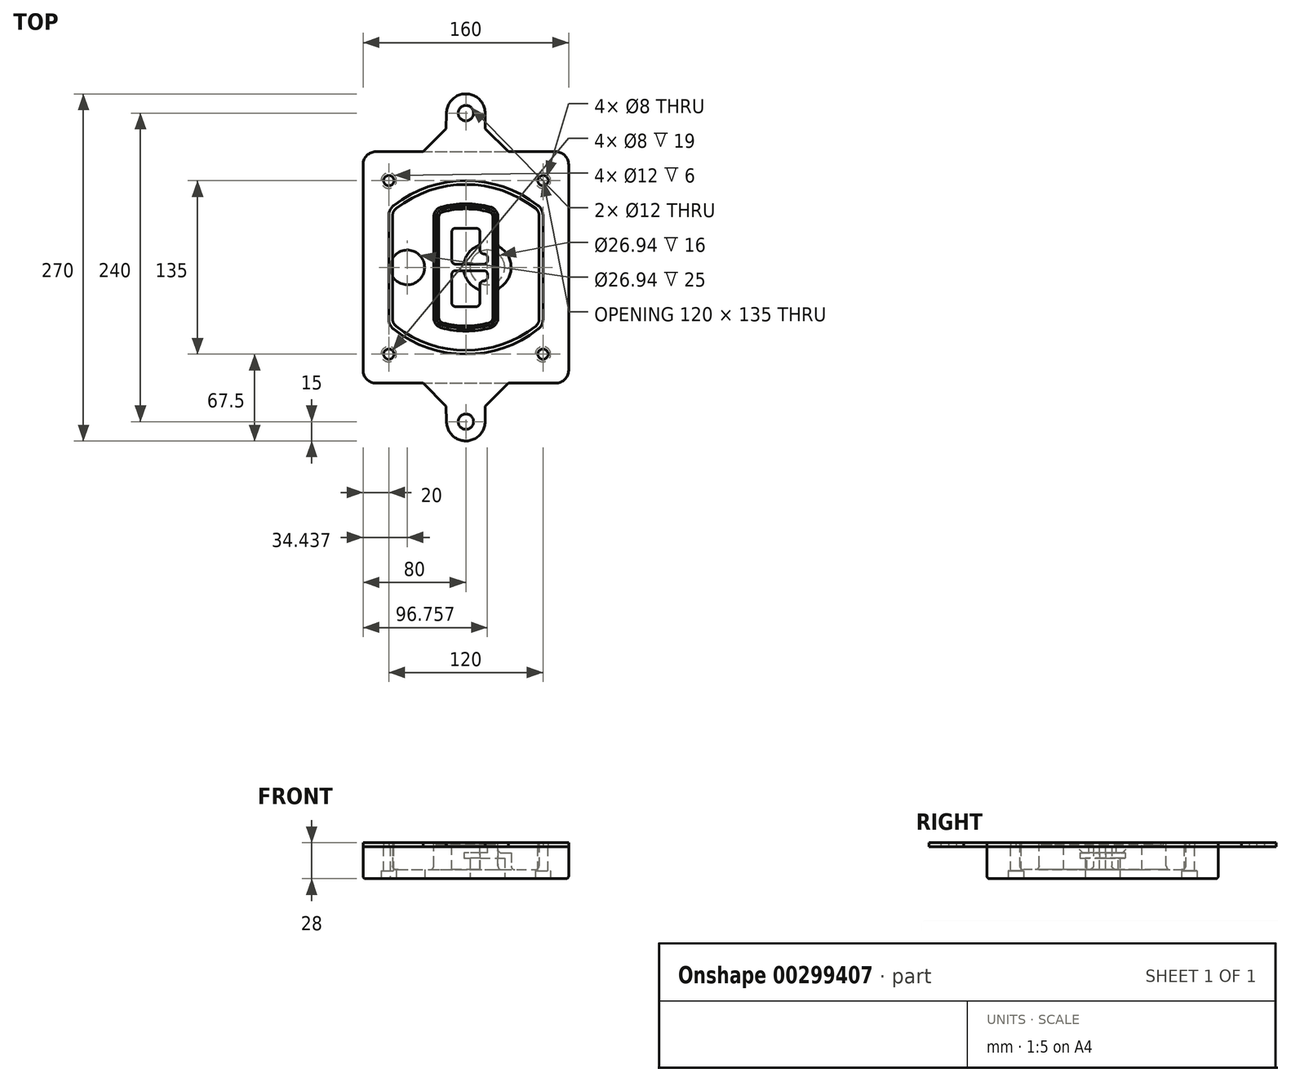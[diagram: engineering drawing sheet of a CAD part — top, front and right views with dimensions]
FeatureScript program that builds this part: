
annotation { "Feature Type Name" : "Feature", "Feature Type Description" : "" }
export const myFeature = defineFeature(function(context is Context, id is Id, definition is map)
    precondition{}
    {
        {
            var Q0;
            Q0=qCreatedBy(makeId("Top.planeOp"),FACE);
            var sketch = newSketch(context, id + "F0", { "sketchPlane" : qUnion([Q0])});
            skPoint(sketch, "E0.rect.middle", {"position": v(0, 0) * mm});
            skLineSegment(sketch, "E1.bottom", {"start": v(-70, -90) * mm, "end": v(70, -90) * mm});
            skLineSegment(sketch, "E1.top", {"start": v(-70, 90) * mm, "end": v(70, 90) * mm});
            skLineSegment(sketch, "E1.left", {"start": v(-80, -80) * mm, "end": v(-80, 80) * mm});
            skLineSegment(sketch, "E1.right", {"start": v(80, -80) * mm, "end": v(80, 80) * mm});
            skLineSegment(sketch, "E2", {"start": v(-80, 90) * mm, "end": v(80, -90) * mm, "construction": true});
            skLineSegment(sketch, "E3", {"start": v(80, 90) * mm, "end": v(-80, -90) * mm, "construction": true});
            skCircle(sketch, "E4", {"center": v(-60, 67.5) * mm, "radius": 4 * mm});
            skCircle(sketch, "E5", {"center": v(60, 67.5) * mm, "radius": 4 * mm});
            skCircle(sketch, "E6", {"center": v(60, -67.5) * mm, "radius": 4 * mm});
            skCircle(sketch, "E7", {"center": v(-60, -67.5) * mm, "radius": 4 * mm});
            skLineSegment(sketch, "E8", {"start": v(-60, 67.5) * mm, "end": v(60, 67.5) * mm, "construction": true});
            skLineSegment(sketch, "E9", {"start": v(60, 67.5) * mm, "end": v(60, -67.5) * mm, "construction": true});
            skLineSegment(sketch, "E10", {"start": v(60, -67.5) * mm, "end": v(-60, -67.5) * mm, "construction": true});
            skLineSegment(sketch, "E11", {"start": v(-60, -67.5) * mm, "end": v(-60, 67.5) * mm, "construction": true});
            skLineSegment(sketch, "E12", {"start": v(-60, 40.3) * mm, "end": v(-60, -40.3) * mm});
            skLineSegment(sketch, "E13", {"start": v(60, 40.3) * mm, "end": v(60, -40.3) * mm});
            skArc(sketch, "E14", {"start": v(56.15, 48.18) * mm, "mid": v(0, 67.5) * mm, "end": v(-56.15, 48.18) * mm});
            skArc(sketch, "E15", {"start": v(-56.15, -48.18) * mm, "mid": v(0, -67.5) * mm, "end": v(56.15, -48.18) * mm});
            skLineSegment(sketch, "E16", {"start": v(-60, 0) * mm, "end": v(60, 0) * mm, "construction": true});
            skPoint(sketch, "E17.visualSharp", {"position": v(-60, -45) * mm});
            skArc(sketch, "E17.filletArc", {"start": v(-60, -40.3) * mm, "mid": v(-58.99, -44.68) * mm, "end": v(-56.15, -48.18) * mm});
            skPoint(sketch, "E18.visualSharp", {"position": v(-60, 45) * mm});
            skArc(sketch, "E18.filletArc", {"start": v(-56.15, 48.18) * mm, "mid": v(-58.99, 44.68) * mm, "end": v(-60, 40.3) * mm});
            skPoint(sketch, "E19.visualSharp", {"position": v(60, 45) * mm});
            skArc(sketch, "E19.filletArc", {"start": v(60, 40.3) * mm, "mid": v(58.99, 44.68) * mm, "end": v(56.15, 48.18) * mm});
            skPoint(sketch, "E20.visualSharp", {"position": v(60, -45) * mm});
            skArc(sketch, "E20.filletArc", {"start": v(56.15, -48.18) * mm, "mid": v(58.99, -44.68) * mm, "end": v(60, -40.3) * mm});
            skPoint(sketch, "E21.visualSharp", {"position": v(-80, 90) * mm});
            skArc(sketch, "E21.filletArc", {"start": v(-70, 90) * mm, "mid": v(-77.07, 87.07) * mm, "end": v(-80, 80) * mm});
            skPoint(sketch, "E22.visualSharp", {"position": v(80, 90) * mm});
            skArc(sketch, "E22.filletArc", {"start": v(80, 80) * mm, "mid": v(77.07, 87.07) * mm, "end": v(70, 90) * mm});
            skPoint(sketch, "E23.visualSharp", {"position": v(80, -90) * mm});
            skArc(sketch, "E23.filletArc", {"start": v(70, -90) * mm, "mid": v(77.07, -87.07) * mm, "end": v(80, -80) * mm});
            skPoint(sketch, "E24.visualSharp", {"position": v(-80, -90) * mm});
            skArc(sketch, "E24.filletArc", {"start": v(-80, -80) * mm, "mid": v(-77.07, -87.07) * mm, "end": v(-70, -90) * mm});
            skArc(sketch, "E25.0", {"start": v(57, 40.3) * mm, "mid": v(56.3, 43.36) * mm, "end": v(54.3, 45.81) * mm});
            skLineSegment(sketch, "E25.1", {"start": v(57, 40.3) * mm, "end": v(57, -40.3) * mm});
            skArc(sketch, "E25.2", {"start": v(54.3, -45.81) * mm, "mid": v(56.3, -43.36) * mm, "end": v(57, -40.3) * mm});
            skArc(sketch, "E25.3", {"start": v(-54.3, -45.81) * mm, "mid": v(0, -64.5) * mm, "end": v(54.3, -45.81) * mm});
            skArc(sketch, "E25.4", {"start": v(-57, -40.3) * mm, "mid": v(-56.3, -43.36) * mm, "end": v(-54.3, -45.81) * mm});
            skArc(sketch, "E25.5", {"start": v(54.3, 45.81) * mm, "mid": v(0, 64.5) * mm, "end": v(-54.3, 45.81) * mm});
            skLineSegment(sketch, "E25.6", {"start": v(-57, 40.3) * mm, "end": v(-57, -40.3) * mm});
            skArc(sketch, "E25.7", {"start": v(-54.3, 45.81) * mm, "mid": v(-56.3, 43.36) * mm, "end": v(-57, 40.3) * mm});
            skArc(sketch, "E26.0", {"start": v(-58.62, 51.33) * mm, "mid": v(-62.58, 46.43) * mm, "end": v(-64, 40.3) * mm});
            skArc(sketch, "E26.1", {"start": v(58.62, 51.33) * mm, "mid": v(0, 71.5) * mm, "end": v(-58.62, 51.33) * mm});
            skArc(sketch, "E26.2", {"start": v(64, 40.3) * mm, "mid": v(62.58, 46.43) * mm, "end": v(58.62, 51.33) * mm});
            skLineSegment(sketch, "E26.3", {"start": v(64, 40.3) * mm, "end": v(64, -40.3) * mm});
            skArc(sketch, "E26.4", {"start": v(58.62, -51.33) * mm, "mid": v(62.58, -46.43) * mm, "end": v(64, -40.3) * mm});
            skLineSegment(sketch, "E26.5", {"start": v(-64, 40.3) * mm, "end": v(-64, -40.3) * mm});
            skArc(sketch, "E26.6", {"start": v(-58.62, -51.33) * mm, "mid": v(0, -71.5) * mm, "end": v(58.62, -51.33) * mm});
            skArc(sketch, "E26.7", {"start": v(-64, -40.3) * mm, "mid": v(-62.58, -46.43) * mm, "end": v(-58.62, -51.33) * mm});
            skSolve(sketch);
        }
        {
            var Q0;
            Q0=makeQuery(id+"F0.imprint","IMPRINT",FACE,{"disambiguationData":[TD([[makeQuery(id+"F0.imprint","IMPRINT",EDGE,{"derivedFrom":sQuery(id+"F0.wireOp",EDGE,"E1.bottom")}),1.0]])]});
            var Q1;
            Q1=makeQuery(id+"F0.imprint","IMPRINT",FACE,{"disambiguationData":[TD([[makeQuery(id+"F0.imprint","IMPRINT",EDGE,{"derivedFrom":sQuery(id+"F0.wireOp",EDGE,"E12")}),1.0]])]});
            var Q2;
            Q2=makeQuery(id+"F0.imprint","IMPRINT",FACE,{"disambiguationData":[TD([[makeQuery(id+"F0.imprint","IMPRINT",EDGE,{"derivedFrom":sQuery(id+"F0.wireOp",EDGE,"E25.0")}),1.0]])]});
            var Q3;
            Q3=makeQuery(id+"F0.imprint","IMPRINT",FACE,{"disambiguationData":[TD([[makeQuery(id+"F0.imprint","IMPRINT",EDGE,{"derivedFrom":sQuery(id+"F0.wireOp",EDGE,"E12")}),-1.0]])]});
            extrude(context, id + "F1", {"entities" : qUnion([Q0, Q1, Q2, Q3]), "oppositeDirection" : true, "depth" : 25 * mm});
        }
        {
            var Q0;
            Q0=makeQuery(id+"F0.imprint","IMPRINT",FACE,{"disambiguationData":[TD([[makeQuery(id+"F0.imprint","IMPRINT",EDGE,{"derivedFrom":sQuery(id+"F0.wireOp",EDGE,"E12")}),1.0]])]});
            extrude(context, id + "F2", {"entities" : qUnion([Q0]), "operationType" : NewBodyOperationType.ADD, "depth" : 3 * mm});
        }
        {
            var Q0;
            Q0=makeQuery(id+"F0.imprint","IMPRINT",FACE,{"disambiguationData":[TD([[makeQuery(id+"F0.imprint","IMPRINT",EDGE,{"derivedFrom":sQuery(id+"F0.wireOp",EDGE,"E25.0")}),1.0]])]});
            extrude(context, id + "F3", {"entities" : qUnion([Q0]), "operationType" : NewBodyOperationType.REMOVE, "oppositeDirection" : true, "depth" : 18 * mm});
        }
        {
            var Q0;
            Q0=makeQuery(id+"F2.opExtrude","CAP_FACE",FACE,{"disambiguationData":[OSD([sQuery(id+"F0.wireOp",EDGE,"E12"),sQuery(id+"F0.wireOp",EDGE,"E13"),sQuery(id+"F0.wireOp",EDGE,"E14"),sQuery(id+"F0.wireOp",EDGE,"E15"),sQuery(id+"F0.wireOp",EDGE,"E17.filletArc"),sQuery(id+"F0.wireOp",EDGE,"E18.filletArc"),sQuery(id+"F0.wireOp",EDGE,"E19.filletArc"),sQuery(id+"F0.wireOp",EDGE,"E20.filletArc"),sQuery(id+"F0.wireOp",EDGE,"E25.0"),sQuery(id+"F0.wireOp",EDGE,"E25.1"),sQuery(id+"F0.wireOp",EDGE,"E25.2"),sQuery(id+"F0.wireOp",EDGE,"E25.3"),sQuery(id+"F0.wireOp",EDGE,"E25.4"),sQuery(id+"F0.wireOp",EDGE,"E25.5"),sQuery(id+"F0.wireOp",EDGE,"E25.6"),sQuery(id+"F0.wireOp",EDGE,"E25.7")])],"isStart":false});
            var sketch = newSketch(context, id + "F4", { "sketchPlane" : qUnion([Q0])});
            skArc(sketch, "E27.0", {"start": v(-19.08, -46.97) * mm, "mid": v(0, -49.5) * mm, "end": v(19.08, -46.97) * mm});
            skArc(sketch, "E28.0", {"start": v(19.08, 46.97) * mm, "mid": v(0, 49.5) * mm, "end": v(-19.08, 46.97) * mm});
            skLineSegment(sketch, "E29", {"start": v(-25, 39.25) * mm, "end": v(-25, -39.25) * mm});
            skLineSegment(sketch, "E30", {"start": v(25, 39.25) * mm, "end": v(25, -39.25) * mm});
            skLineSegment(sketch, "E31", {"start": v(-25, 45.1) * mm, "end": v(25, 45.1) * mm, "construction": true});
            skLineSegment(sketch, "E32", {"start": v(-25, -45.1) * mm, "end": v(25, -45.1) * mm, "construction": true});
            skPoint(sketch, "E33.visualSharp", {"position": v(-25, 45.1) * mm});
            skArc(sketch, "E33.filletArc", {"start": v(-19.08, 46.97) * mm, "mid": v(-23.35, 44.11) * mm, "end": v(-25, 39.25) * mm});
            skPoint(sketch, "E34.visualSharp", {"position": v(25, 45.1) * mm});
            skArc(sketch, "E34.filletArc", {"start": v(25, 39.25) * mm, "mid": v(23.35, 44.11) * mm, "end": v(19.08, 46.97) * mm});
            skPoint(sketch, "E35.visualSharp", {"position": v(25, -45.1) * mm});
            skArc(sketch, "E35.filletArc", {"start": v(19.08, -46.97) * mm, "mid": v(23.35, -44.11) * mm, "end": v(25, -39.25) * mm});
            skPoint(sketch, "E36.visualSharp", {"position": v(-25, -45.1) * mm});
            skArc(sketch, "E36.filletArc", {"start": v(-25, -39.25) * mm, "mid": v(-23.35, -44.11) * mm, "end": v(-19.08, -46.97) * mm});
            skArc(sketch, "E37.0", {"start": v(54.3, 45.81) * mm, "mid": v(0, 64.5) * mm, "end": v(-54.3, 45.81) * mm});
            skArc(sketch, "E37.1", {"start": v(-54.3, 45.81) * mm, "mid": v(-56.3, 43.36) * mm, "end": v(-57, 40.3) * mm});
            skLineSegment(sketch, "E37.2", {"start": v(-57, 40.3) * mm, "end": v(-57, -40.3) * mm});
            skArc(sketch, "E37.3", {"start": v(-57, -40.3) * mm, "mid": v(-56.3, -43.36) * mm, "end": v(-54.3, -45.81) * mm});
            skArc(sketch, "E37.4", {"start": v(-54.3, -45.81) * mm, "mid": v(0, -64.5) * mm, "end": v(54.3, -45.81) * mm});
            skArc(sketch, "E37.5", {"start": v(54.3, -45.81) * mm, "mid": v(56.3, -43.36) * mm, "end": v(57, -40.3) * mm});
            skLineSegment(sketch, "E37.6", {"start": v(57, 40.3) * mm, "end": v(57, -40.3) * mm});
            skArc(sketch, "E37.7", {"start": v(57, 40.3) * mm, "mid": v(56.3, 43.36) * mm, "end": v(54.3, 45.81) * mm});
            skLineSegment(sketch, "E38.0", {"start": v(23, 39.25) * mm, "end": v(23, -39.25) * mm});
            skArc(sketch, "E38.1", {"start": v(18.56, -45.04) * mm, "mid": v(21.76, -42.9) * mm, "end": v(23, -39.25) * mm});
            skArc(sketch, "E38.2", {"start": v(-18.56, -45.04) * mm, "mid": v(0, -47.5) * mm, "end": v(18.56, -45.04) * mm});
            skArc(sketch, "E38.3", {"start": v(-23, -39.25) * mm, "mid": v(-21.76, -42.9) * mm, "end": v(-18.56, -45.04) * mm});
            skLineSegment(sketch, "E38.4", {"start": v(-23, 39.25) * mm, "end": v(-23, -39.25) * mm});
            skArc(sketch, "E38.5", {"start": v(23, 39.25) * mm, "mid": v(21.76, 42.9) * mm, "end": v(18.56, 45.04) * mm});
            skArc(sketch, "E38.6", {"start": v(-18.56, 45.04) * mm, "mid": v(-21.76, 42.9) * mm, "end": v(-23, 39.25) * mm});
            skArc(sketch, "E38.7", {"start": v(18.56, 45.04) * mm, "mid": v(0, 47.5) * mm, "end": v(-18.56, 45.04) * mm});
            skArc(sketch, "E39.0", {"start": v(21, 39.25) * mm, "mid": v(20.18, 41.68) * mm, "end": v(18.04, 43.1) * mm});
            skLineSegment(sketch, "E39.1", {"start": v(21, 39.25) * mm, "end": v(21, -39.25) * mm});
            skArc(sketch, "E39.2", {"start": v(18.04, -43.1) * mm, "mid": v(20.18, -41.68) * mm, "end": v(21, -39.25) * mm});
            skArc(sketch, "E39.3", {"start": v(-18.04, -43.1) * mm, "mid": v(0, -45.5) * mm, "end": v(18.04, -43.1) * mm});
            skArc(sketch, "E39.4", {"start": v(-21, -39.25) * mm, "mid": v(-20.18, -41.68) * mm, "end": v(-18.04, -43.1) * mm});
            skArc(sketch, "E39.5", {"start": v(18.04, 43.1) * mm, "mid": v(0, 45.5) * mm, "end": v(-18.04, 43.1) * mm});
            skLineSegment(sketch, "E39.6", {"start": v(-21, 39.25) * mm, "end": v(-21, -39.25) * mm});
            skArc(sketch, "E39.7", {"start": v(-18.04, 43.1) * mm, "mid": v(-20.18, 41.68) * mm, "end": v(-21, 39.25) * mm});
            skLineSegment(sketch, "E40", {"start": v(-25, 0) * mm, "end": v(25, 0) * mm, "construction": true});
            skLineSegment(sketch, "E41", {"start": v(-11, 5.5) * mm, "end": v(-11, 27.5) * mm});
            skLineSegment(sketch, "E42", {"start": v(-8, 30.5) * mm, "end": v(8, 30.5) * mm});
            skLineSegment(sketch, "E43", {"start": v(11, 27.5) * mm, "end": v(11, 13.5) * mm});
            skLineSegment(sketch, "E44", {"start": v(14, 10.5) * mm, "end": v(14, 10.5) * mm});
            skLineSegment(sketch, "E45", {"start": v(17, 7.5) * mm, "end": v(17, 5.5) * mm});
            skLineSegment(sketch, "E46", {"start": v(14, 2.5) * mm, "end": v(-8, 2.5) * mm});
            skPoint(sketch, "E47.visualSharp", {"position": v(-11, 30.5) * mm});
            skArc(sketch, "E47.filletArc", {"start": v(-8, 30.5) * mm, "mid": v(-10.12, 29.62) * mm, "end": v(-11, 27.5) * mm});
            skPoint(sketch, "E48.visualSharp", {"position": v(11, 30.5) * mm});
            skArc(sketch, "E48.filletArc", {"start": v(11, 27.5) * mm, "mid": v(10.12, 29.62) * mm, "end": v(8, 30.5) * mm});
            skPoint(sketch, "E49.visualSharp", {"position": v(11, 10.5) * mm});
            skArc(sketch, "E49.filletArc", {"start": v(11, 13.5) * mm, "mid": v(11.88, 11.38) * mm, "end": v(14, 10.5) * mm});
            skPoint(sketch, "E50.visualSharp", {"position": v(17, 10.5) * mm});
            skArc(sketch, "E50.filletArc", {"start": v(17, 7.5) * mm, "mid": v(16.12, 9.62) * mm, "end": v(14, 10.5) * mm});
            skPoint(sketch, "E51.visualSharp", {"position": v(17, 2.5) * mm});
            skArc(sketch, "E51.filletArc", {"start": v(14, 2.5) * mm, "mid": v(16.12, 3.38) * mm, "end": v(17, 5.5) * mm});
            skPoint(sketch, "E52.visualSharp", {"position": v(-11, 2.5) * mm});
            skArc(sketch, "E52.filletArc", {"start": v(-11, 5.5) * mm, "mid": v(-10.12, 3.38) * mm, "end": v(-8, 2.5) * mm});
            skLineSegment(sketch, "E53.0.MirrorCS", {"start": v(14, -2.5) * mm, "end": v(-8, -2.5) * mm});
            skArc(sketch, "E54.0.MirrorCS", {"start": v(-11, -5.5) * mm, "mid": v(-10.12, -3.38) * mm, "end": v(-8, -2.5) * mm});
            skLineSegment(sketch, "E55.0.MirrorCS", {"start": v(-11, -5.5) * mm, "end": v(-11, -27.5) * mm});
            skArc(sketch, "E56.0.MirrorCS", {"start": v(-8, -30.5) * mm, "mid": v(-10.12, -29.62) * mm, "end": v(-11, -27.5) * mm});
            skLineSegment(sketch, "E57.0.MirrorCS", {"start": v(-8, -30.5) * mm, "end": v(8, -30.5) * mm});
            skArc(sketch, "E58.0.MirrorCS", {"start": v(11, -27.5) * mm, "mid": v(10.12, -29.62) * mm, "end": v(8, -30.5) * mm});
            skLineSegment(sketch, "E59.0.MirrorCS", {"start": v(11, -27.5) * mm, "end": v(11, -13.5) * mm});
            skArc(sketch, "E60.0.MirrorCS", {"start": v(11, -13.5) * mm, "mid": v(11.88, -11.38) * mm, "end": v(14, -10.5) * mm});
            skArc(sketch, "E61.0.MirrorCS", {"start": v(17, -7.5) * mm, "mid": v(16.12, -9.62) * mm, "end": v(14, -10.5) * mm});
            skLineSegment(sketch, "E62.0.MirrorCS", {"start": v(17, -7.5) * mm, "end": v(17, -5.5) * mm});
            skArc(sketch, "E63.0.MirrorCS", {"start": v(14, -2.5) * mm, "mid": v(16.12, -3.38) * mm, "end": v(17, -5.5) * mm});
            skSolve(sketch);
        }
        {
            var Q0;
            Q0=makeQuery(id+"F4.imprint","IMPRINT",FACE,{"disambiguationData":[TD([[makeQuery(id+"F4.imprint","IMPRINT",EDGE,{"derivedFrom":sQuery(id+"F4.wireOp",EDGE,"E27.0")}),1.0]])]});
            var Q1;
            Q1=makeQuery(id+"F4.imprint","IMPRINT",FACE,{"disambiguationData":[TD([[makeQuery(id+"F4.imprint","IMPRINT",EDGE,{"derivedFrom":sQuery(id+"F4.wireOp",EDGE,"E38.0")}),-1.0]])]});
            var Q2;
            Q2=makeQuery(id+"F4.imprint","IMPRINT",FACE,{"disambiguationData":[TD([[makeQuery(id+"F4.imprint","IMPRINT",EDGE,{"derivedFrom":sQuery(id+"F4.wireOp",EDGE,"E39.0")}),1.0]])]});
            extrude(context, id + "F5", {"entities" : qUnion([Q0, Q1, Q2]), "operationType" : NewBodyOperationType.ADD, "endBound" : BoundingType.UP_TO_NEXT, "oppositeDirection" : true, "depth" : 25 * mm});
        }
        {
            var Q0;
            Q0=makeQuery(id+"F4.imprint","IMPRINT",FACE,{"disambiguationData":[TD([[makeQuery(id+"F4.imprint","IMPRINT",EDGE,{"derivedFrom":sQuery(id+"F4.wireOp",EDGE,"E38.0")}),-1.0]])]});
            extrude(context, id + "F6", {"entities" : qUnion([Q0]), "operationType" : NewBodyOperationType.REMOVE, "oppositeDirection" : true, "depth" : 2 * mm});
        }
        {
            var Q0;
            Q0=makeQuery(id+"F1.opExtrude","CAP_FACE",FACE,{"disambiguationData":[OSD([sQuery(id+"F0.wireOp",EDGE,"E1.bottom"),sQuery(id+"F0.wireOp",EDGE,"E1.top"),sQuery(id+"F0.wireOp",EDGE,"E1.left"),sQuery(id+"F0.wireOp",EDGE,"E1.right"),sQuery(id+"F0.wireOp",EDGE,"E4"),sQuery(id+"F0.wireOp",EDGE,"E5"),sQuery(id+"F0.wireOp",EDGE,"E6"),sQuery(id+"F0.wireOp",EDGE,"E7"),sQuery(id+"F0.wireOp",EDGE,"E21.filletArc"),sQuery(id+"F0.wireOp",EDGE,"E22.filletArc"),sQuery(id+"F0.wireOp",EDGE,"E23.filletArc"),sQuery(id+"F0.wireOp",EDGE,"E24.filletArc")])],"isStart":false});
            var sketch = newSketch(context, id + "F7", { "sketchPlane" : qUnion([Q0])});
            skCircle(sketch, "E64", {"center": v(16.76, 0) * mm, "radius": 13.47 * mm});
            skCircle(sketch, "E65", {"center": v(-45.56, 0) * mm, "radius": 13.47 * mm});
            skLineSegment(sketch, "E66", {"start": v(80, 0) * mm, "end": v(-80, 0) * mm});
            skCircle(sketch, "E67", {"center": v(16.76, 0) * mm, "radius": 18.47 * mm});
            skCircle(sketch, "E68", {"center": v(60, -67.5) * mm, "radius": 6 * mm});
            skCircle(sketch, "E69", {"center": v(-60, -67.5) * mm, "radius": 6 * mm});
            skCircle(sketch, "E70", {"center": v(-60, 67.5) * mm, "radius": 6 * mm});
            skCircle(sketch, "E71", {"center": v(60, 67.5) * mm, "radius": 6 * mm});
            skSolve(sketch);
        }
        {
            var Q0;
            {var subQ1=sQuery(id+"F7.wireOp",EDGE,"E66");var subQ4=sQuery(id+"F7.wireOp",EDGE,"E64");var subQ6=makeQuery(id+"F7.imprint","INTERSECT",VERTEX,{"disambiguationData":[OD(0.0)],"derivedFrom":[subQ4,subQ1]});Q0=makeQuery(id+"F7.imprint","IMPRINT",FACE,{"disambiguationData":[TD([[makeQuery(id+"F7.imprint","IMPRINT",EDGE,{"disambiguationData":[TD([[subQ6,-1.0]])],"derivedFrom":subQ4}),-1.0]])]});}
            var Q1;
            {var subQ0=sQuery(id+"F7.wireOp",EDGE,"E66");var subQ1=sQuery(id+"F7.wireOp",EDGE,"E64");var subQ3=makeQuery(id+"F7.imprint","INTERSECT",VERTEX,{"disambiguationData":[OD(0.0)],"derivedFrom":[subQ1,subQ0]});Q1=makeQuery(id+"F7.imprint","IMPRINT",FACE,{"disambiguationData":[TD([[makeQuery(id+"F7.imprint","IMPRINT",EDGE,{"disambiguationData":[TD([[subQ3,-1.0]])],"derivedFrom":subQ1}),1.0]])]});}
            var Q2;
            {var subQ0=sQuery(id+"F7.wireOp",EDGE,"E66");var subQ1=sQuery(id+"F7.wireOp",EDGE,"E64");var subQ3=makeQuery(id+"F7.imprint","INTERSECT",VERTEX,{"disambiguationData":[OD(0.0)],"derivedFrom":[subQ1,subQ0]});Q2=makeQuery(id+"F7.imprint","IMPRINT",FACE,{"disambiguationData":[TD([[makeQuery(id+"F7.imprint","IMPRINT",EDGE,{"disambiguationData":[TD([[subQ3,1.0]])],"derivedFrom":subQ1}),1.0]])]});}
            var Q3;
            {var subQ1=sQuery(id+"F7.wireOp",EDGE,"E66");var subQ4=sQuery(id+"F7.wireOp",EDGE,"E64");var subQ6=makeQuery(id+"F7.imprint","INTERSECT",VERTEX,{"disambiguationData":[OD(0.0)],"derivedFrom":[subQ4,subQ1]});Q3=makeQuery(id+"F7.imprint","IMPRINT",FACE,{"disambiguationData":[TD([[makeQuery(id+"F7.imprint","IMPRINT",EDGE,{"disambiguationData":[TD([[subQ6,1.0]])],"derivedFrom":subQ4}),-1.0]])]});}
            extrude(context, id + "F8", {"entities" : qUnion([Q0, Q1, Q2, Q3]), "operationType" : NewBodyOperationType.ADD, "oppositeDirection" : true, "depth" : 20 * mm});
        }
        {
            var Q0;
            {var subQ0=sQuery(id+"F7.wireOp",EDGE,"E66");var subQ1=sQuery(id+"F7.wireOp",EDGE,"E64");var subQ3=makeQuery(id+"F7.imprint","INTERSECT",VERTEX,{"disambiguationData":[OD(0.0)],"derivedFrom":[subQ1,subQ0]});Q0=makeQuery(id+"F7.imprint","IMPRINT",FACE,{"disambiguationData":[TD([[makeQuery(id+"F7.imprint","IMPRINT",EDGE,{"disambiguationData":[TD([[subQ3,-1.0]])],"derivedFrom":subQ1}),1.0]])]});}
            var Q1;
            {var subQ0=sQuery(id+"F7.wireOp",EDGE,"E66");var subQ1=sQuery(id+"F7.wireOp",EDGE,"E64");var subQ3=makeQuery(id+"F7.imprint","INTERSECT",VERTEX,{"disambiguationData":[OD(0.0)],"derivedFrom":[subQ1,subQ0]});Q1=makeQuery(id+"F7.imprint","IMPRINT",FACE,{"disambiguationData":[TD([[makeQuery(id+"F7.imprint","IMPRINT",EDGE,{"disambiguationData":[TD([[subQ3,1.0]])],"derivedFrom":subQ1}),1.0]])]});}
            extrude(context, id + "F9", {"entities" : qUnion([Q0, Q1]), "operationType" : NewBodyOperationType.REMOVE, "oppositeDirection" : true, "depth" : 16 * mm});
        }
        {
            var Q0;
            {var subQ0=sQuery(id+"F7.wireOp",EDGE,"E66");var subQ1=sQuery(id+"F7.wireOp",EDGE,"E65");var subQ3=makeQuery(id+"F7.imprint","INTERSECT",VERTEX,{"disambiguationData":[OD(0.0)],"derivedFrom":[subQ1,subQ0]});Q0=makeQuery(id+"F7.imprint","IMPRINT",FACE,{"disambiguationData":[TD([[makeQuery(id+"F7.imprint","IMPRINT",EDGE,{"disambiguationData":[TD([[subQ3,-1.0]])],"derivedFrom":subQ1}),1.0]])]});}
            var Q1;
            {var subQ0=sQuery(id+"F7.wireOp",EDGE,"E66");var subQ1=sQuery(id+"F7.wireOp",EDGE,"E65");var subQ3=makeQuery(id+"F7.imprint","INTERSECT",VERTEX,{"disambiguationData":[OD(0.0)],"derivedFrom":[subQ1,subQ0]});Q1=makeQuery(id+"F7.imprint","IMPRINT",FACE,{"disambiguationData":[TD([[makeQuery(id+"F7.imprint","IMPRINT",EDGE,{"disambiguationData":[TD([[subQ3,1.0]])],"derivedFrom":subQ1}),1.0]])]});}
            extrude(context, id + "F10", {"entities" : qUnion([Q0, Q1]), "operationType" : NewBodyOperationType.REMOVE, "oppositeDirection" : true, "depth" : 25 * mm});
        }
        {
            var Q0;
            Q0=makeQuery(id+"F7.imprint","IMPRINT",FACE,{"disambiguationData":[TD([[makeQuery(id+"F7.imprint","IMPRINT",EDGE,{"derivedFrom":sQuery(id+"F7.wireOp",EDGE,"E68")}),1.0]])]});
            var Q1;
            Q1=makeQuery(id+"F7.imprint","IMPRINT",FACE,{"disambiguationData":[TD([[makeQuery(id+"F7.imprint","IMPRINT",EDGE,{"derivedFrom":makeQuery(id+"F1.opExtrude","CAP_EDGE",EDGE,{"disambiguationData":[OSD([sQuery(id+"F0.wireOp",EDGE,"E5")])],"isStart":false})}),-1.0]])]});
            var Q2;
            Q2=makeQuery(id+"F7.imprint","IMPRINT",FACE,{"disambiguationData":[TD([[makeQuery(id+"F7.imprint","IMPRINT",EDGE,{"derivedFrom":sQuery(id+"F7.wireOp",EDGE,"E69")}),1.0]])]});
            var Q3;
            Q3=makeQuery(id+"F7.imprint","IMPRINT",FACE,{"disambiguationData":[TD([[makeQuery(id+"F7.imprint","IMPRINT",EDGE,{"derivedFrom":makeQuery(id+"F1.opExtrude","CAP_EDGE",EDGE,{"disambiguationData":[OSD([sQuery(id+"F0.wireOp",EDGE,"E4")])],"isStart":false})}),-1.0]])]});
            var Q4;
            Q4=makeQuery(id+"F7.imprint","IMPRINT",FACE,{"disambiguationData":[TD([[makeQuery(id+"F7.imprint","IMPRINT",EDGE,{"derivedFrom":sQuery(id+"F7.wireOp",EDGE,"E70")}),1.0]])]});
            var Q5;
            Q5=makeQuery(id+"F7.imprint","IMPRINT",FACE,{"disambiguationData":[TD([[makeQuery(id+"F7.imprint","IMPRINT",EDGE,{"derivedFrom":makeQuery(id+"F1.opExtrude","CAP_EDGE",EDGE,{"disambiguationData":[OSD([sQuery(id+"F0.wireOp",EDGE,"E7")])],"isStart":false})}),-1.0]])]});
            var Q6;
            Q6=makeQuery(id+"F7.imprint","IMPRINT",FACE,{"disambiguationData":[TD([[makeQuery(id+"F7.imprint","IMPRINT",EDGE,{"derivedFrom":sQuery(id+"F7.wireOp",EDGE,"E71")}),1.0]])]});
            var Q7;
            Q7=makeQuery(id+"F7.imprint","IMPRINT",FACE,{"disambiguationData":[TD([[makeQuery(id+"F7.imprint","IMPRINT",EDGE,{"derivedFrom":makeQuery(id+"F1.opExtrude","CAP_EDGE",EDGE,{"disambiguationData":[OSD([sQuery(id+"F0.wireOp",EDGE,"E6")])],"isStart":false})}),-1.0]])]});
            extrude(context, id + "F11", {"entities" : qUnion([Q0, Q1, Q2, Q3, Q4, Q5, Q6, Q7]), "operationType" : NewBodyOperationType.REMOVE, "oppositeDirection" : true, "depth" : 6 * mm});
        }
        {
            var Q0;
            Q0=makeQuery(id+"F9.boolean.opBoolean","COPY",FACE,{"derivedFrom":makeQuery(id+"F9.opExtrude","CAP_FACE",FACE,{"disambiguationData":[OSD([sQuery(id+"F7.wireOp",EDGE,"E64")])],"isStart":false})});
            var sketch = newSketch(context, id + "F12", { "sketchPlane" : qUnion([Q0])});
            skArc(sketch, "E72.0", {"start": v(11, 17.55) * mm, "mid": v(2.57, 11.82) * mm, "end": v(-1.54, 2.5) * mm});
            skArc(sketch, "E72.1", {"start": v(-1.54, -2.5) * mm, "mid": v(2.57, -11.82) * mm, "end": v(11, -17.55) * mm});
            skLineSegment(sketch, "E73", {"start": v(-1.54, -2.5) * mm, "end": v(14, -2.5) * mm});
            skLineSegment(sketch, "E74.0", {"start": v(14, 2.5) * mm, "end": v(-1.54, 2.5) * mm});
            skArc(sketch, "E74.1", {"start": v(14, 2.5) * mm, "mid": v(16.12, 3.38) * mm, "end": v(17, 5.5) * mm});
            skLineSegment(sketch, "E74.2", {"start": v(17, 7.5) * mm, "end": v(17, 5.5) * mm});
            skArc(sketch, "E74.3", {"start": v(17, 7.5) * mm, "mid": v(16.12, 9.62) * mm, "end": v(14, 10.5) * mm});
            skArc(sketch, "E74.4", {"start": v(11, 13.5) * mm, "mid": v(11.88, 11.38) * mm, "end": v(14, 10.5) * mm});
            skLineSegment(sketch, "E74.5", {"start": v(11, 17.55) * mm, "end": v(11, 13.5) * mm});
            skLineSegment(sketch, "E74.7", {"start": v(14, -2.5) * mm, "end": v(-1.54, -2.5) * mm});
            skArc(sketch, "E74.8", {"start": v(14, -2.5) * mm, "mid": v(16.12, -3.38) * mm, "end": v(17, -5.5) * mm});
            skLineSegment(sketch, "E74.9", {"start": v(17, -7.5) * mm, "end": v(17, -5.5) * mm});
            skArc(sketch, "E74.10", {"start": v(17, -7.5) * mm, "mid": v(16.12, -9.62) * mm, "end": v(14, -10.5) * mm});
            skArc(sketch, "E74.11", {"start": v(11, -13.5) * mm, "mid": v(11.88, -11.38) * mm, "end": v(14, -10.5) * mm});
            skLineSegment(sketch, "E74.12", {"start": v(11, -17.55) * mm, "end": v(11, -13.5) * mm});
            skPoint(sketch, "E75.orphan", {"position": v(11, -27.5) * mm});
            skPoint(sketch, "E76.orphan", {"position": v(-8, -2.5) * mm});
            skPoint(sketch, "E77.orphan", {"position": v(-8, 2.5) * mm});
            skPoint(sketch, "E78.orphan", {"position": v(11, 27.5) * mm});
            skSolve(sketch);
        }
        {
            var Q0;
            {var subQ7=sQuery(id+"F12.wireOp",EDGE,"E72.0");var subQ14=sQuery(id+"F12.wireOp",EDGE,"E72.1");var subQ16=sQuery(id+"F12.wireOp",EDGE,"E74.1");var subQ18=sQuery(id+"F12.wireOp",EDGE,"E74.8");Q0=qUnion([makeQuery(id+"F12.imprint","IMPRINT",FACE,{"disambiguationData":[TD([[makeQuery(id+"F12.imprint","IMPRINT",EDGE,{"derivedFrom":subQ7}),1.0]])]}),makeQuery(id+"F12.imprint","IMPRINT",FACE,{"disambiguationData":[TD([[makeQuery(id+"F12.imprint","IMPRINT",EDGE,{"derivedFrom":subQ14}),1.0]])]}),makeQuery(id+"F12.imprint","IMPRINT",FACE,{"disambiguationData":[TD([[makeQuery(id+"F12.imprint","IMPRINT",EDGE,{"derivedFrom":subQ16}),1.0]])]}),makeQuery(id+"F12.imprint","IMPRINT",FACE,{"disambiguationData":[TD([[makeQuery(id+"F12.imprint","IMPRINT",EDGE,{"derivedFrom":subQ18}),-1.0]])]})]);}
            var Q1;
            Q1=makeQuery(id+"F5.boolean.opBoolean","SPLIT",FACE,{"disambiguationData":[TD([makeQuery(id+"F5.opExtrude","SWEPT_FACE",FACE,{"disambiguationData":[OSD([sQuery(id+"F4.wireOp",EDGE,"E41")])]})])],"derivedFrom":makeQuery(id+"F3.boolean.opBoolean","COPY",FACE,{"derivedFrom":makeQuery(id+"F3.opExtrude","CAP_FACE",FACE,{"disambiguationData":[OSD([sQuery(id+"F0.wireOp",EDGE,"E25.0"),sQuery(id+"F0.wireOp",EDGE,"E25.1"),sQuery(id+"F0.wireOp",EDGE,"E25.2"),sQuery(id+"F0.wireOp",EDGE,"E25.3"),sQuery(id+"F0.wireOp",EDGE,"E25.4"),sQuery(id+"F0.wireOp",EDGE,"E25.5"),sQuery(id+"F0.wireOp",EDGE,"E25.6"),sQuery(id+"F0.wireOp",EDGE,"E25.7")])],"isStart":false})})});
            extrude(context, id + "F13", {"entities" : qUnion([Q0]), "operationType" : NewBodyOperationType.REMOVE, "endBound" : BoundingType.UP_TO_SURFACE, "endBoundEntityFace" : qUnion([Q1]), "depth" : 25 * mm});
        }
        {
            var Q0;
            Q0=makeQuery(id+"F3.boolean.opBoolean","COPY",EDGE,{"derivedFrom":makeQuery(id+"F3.opExtrude","CAP_EDGE",EDGE,{"disambiguationData":[OSD([sQuery(id+"F0.wireOp",EDGE,"E25.6")])],"isStart":false})});
            var Q1;
            Q1=makeQuery(id+"F8.boolean.opBoolean","INTERSECT",EDGE,{"derivedFrom":[makeQuery(id+"F5.opExtrude","SWEPT_FACE",FACE,{"disambiguationData":[OSD([sQuery(id+"F4.wireOp",EDGE,"E30")])]}),makeQuery(id+"F8.opExtrude","CAP_FACE",FACE,{"disambiguationData":[OSD([sQuery(id+"F7.wireOp",EDGE,"E67")])],"isStart":false})]});
            var Q2;
            Q2=makeQuery(id+"F8.boolean.opBoolean","INTERSECT",EDGE,{"disambiguationData":[OD(1.0)],"derivedFrom":[makeQuery(id+"F5.opExtrude","SWEPT_FACE",FACE,{"disambiguationData":[OSD([sQuery(id+"F4.wireOp",EDGE,"E30")])]}),makeQuery(id+"F8.opExtrude","SWEPT_FACE",FACE,{"disambiguationData":[OSD([sQuery(id+"F7.wireOp",EDGE,"E67")])]})]});
            var Q3;
            {var subQ0=sQuery(id+"F4.wireOp",EDGE,"E30");Q3=makeQuery(id+"F8.boolean.opBoolean","SPLIT",EDGE,{"disambiguationData":[TD([makeQuery(id+"F5.opExtrude","SWEPT_FACE",FACE,{"disambiguationData":[OSD([sQuery(id+"F4.wireOp",EDGE,"E35.filletArc")])]})])],"derivedFrom":makeQuery(id+"F5.opExtrude","CAP_EDGE",EDGE,{"disambiguationData":[OSD([subQ0])],"isStart":false})});}
            var Q4;
            {var subQ0=sQuery(id+"F0.wireOp",EDGE,"E25.7");var subQ1=sQuery(id+"F0.wireOp",EDGE,"E25.1");var subQ2=sQuery(id+"F0.wireOp",EDGE,"E25.6");var subQ3=sQuery(id+"F0.wireOp",EDGE,"E25.5");var subQ4=sQuery(id+"F0.wireOp",EDGE,"E25.4");var subQ5=sQuery(id+"F0.wireOp",EDGE,"E25.0");var subQ6=sQuery(id+"F0.wireOp",EDGE,"E25.2");var subQ7=sQuery(id+"F0.wireOp",EDGE,"E25.3");Q4=makeQuery(id+"F8.boolean.opBoolean","INTERSECT",EDGE,{"derivedFrom":[makeQuery(id+"F5.boolean.opBoolean","SPLIT",FACE,{"disambiguationData":[TD([makeQuery(id+"F2.opExtrude","SWEPT_FACE",FACE,{"disambiguationData":[OSD([subQ5])]})])],"derivedFrom":makeQuery(id+"F3.boolean.opBoolean","COPY",FACE,{"derivedFrom":makeQuery(id+"F3.opExtrude","CAP_FACE",FACE,{"disambiguationData":[OSD([subQ5,subQ1,subQ6,subQ7,subQ4,subQ3,subQ2,subQ0])],"isStart":false})})}),makeQuery(id+"F8.opExtrude","SWEPT_FACE",FACE,{"disambiguationData":[OSD([sQuery(id+"F7.wireOp",EDGE,"E67")])]})]});}
            var Q5;
            Q5=makeQuery(id+"F8.boolean.opBoolean","INTERSECT",EDGE,{"disambiguationData":[OD(0.0)],"derivedFrom":[makeQuery(id+"F5.opExtrude","SWEPT_FACE",FACE,{"disambiguationData":[OSD([sQuery(id+"F4.wireOp",EDGE,"E30")])]}),makeQuery(id+"F8.opExtrude","SWEPT_FACE",FACE,{"disambiguationData":[OSD([sQuery(id+"F7.wireOp",EDGE,"E67")])]})]});
            fillet(context, id + "F14", {"entities" : qUnion([Q0, Q1, Q2, Q3, Q4, Q5]), "radius" : 3 * mm, "tangentPropagation" : true, "allowEdgeOverflow" : false});
        }
        {
            var Q0;
            Q0=makeQuery(id+"F1.opExtrude","CAP_EDGE",EDGE,{"disambiguationData":[OSD([sQuery(id+"F0.wireOp",EDGE,"E1.bottom")])],"isStart":false});
            fillet(context, id + "F15", {"entities" : qUnion([Q0]), "radius" : 2 * mm, "tangentPropagation" : true, "allowEdgeOverflow" : false});
        }
        {
            var Q0;
            {var subQ0=sQuery(id+"F0.wireOp",EDGE,"E21.filletArc");var subQ1=sQuery(id+"F0.wireOp",EDGE,"E7");var subQ2=sQuery(id+"F0.wireOp",EDGE,"E6");var subQ3=sQuery(id+"F0.wireOp",EDGE,"E5");var subQ4=sQuery(id+"F0.wireOp",EDGE,"E4");var subQ5=sQuery(id+"F0.wireOp",EDGE,"E22.filletArc");var subQ6=sQuery(id+"F0.wireOp",EDGE,"E1.bottom");var subQ7=sQuery(id+"F0.wireOp",EDGE,"E1.right");var subQ8=sQuery(id+"F0.wireOp",EDGE,"E1.top");var subQ9=sQuery(id+"F0.wireOp",EDGE,"E1.left");var subQ10=sQuery(id+"F0.wireOp",EDGE,"E23.filletArc");var subQ11=sQuery(id+"F0.wireOp",EDGE,"E24.filletArc");Q0=makeQuery(id+"F2.boolean.opBoolean","SPLIT",FACE,{"disambiguationData":[TD([makeQuery(id+"F1.opExtrude","SWEPT_FACE",FACE,{"disambiguationData":[OSD([subQ6])]})])],"derivedFrom":makeQuery(id+"F1.opExtrude","CAP_FACE",FACE,{"disambiguationData":[OSD([subQ6,subQ8,subQ9,subQ7,subQ4,subQ3,subQ2,subQ1,subQ0,subQ5,subQ10,subQ11])],"isStart":true})});}
            var sketch = newSketch(context, id + "F16", { "sketchPlane" : qUnion([Q0])});
            skLineSegment(sketch, "E79", {"start": v(0, 120) * mm, "end": v(0, 90) * mm, "construction": true});
            skCircle(sketch, "E80", {"center": v(0, 120) * mm, "radius": 6 * mm});
            skArc(sketch, "E81", {"start": v(15, 120.03) * mm, "mid": v(-0.1, 135) * mm, "end": v(-15, 119.83) * mm});
            skLineSegment(sketch, "E82", {"start": v(-15, 119.83) * mm, "end": v(-15.37, 108) * mm});
            skLineSegment(sketch, "E83", {"start": v(15, 120.03) * mm, "end": v(15.02, 108) * mm});
            skLineSegment(sketch, "E84", {"start": v(-15.37, 108) * mm, "end": v(-33.37, 90) * mm});
            skLineSegment(sketch, "E85", {"start": v(15.02, 108) * mm, "end": v(33.02, 90) * mm});
            skLineSegment(sketch, "E86", {"start": v(-80, 0) * mm, "end": v(80, 0) * mm, "construction": true});
            skLineSegment(sketch, "E87.MirrorCS", {"start": v(-15, -119.83) * mm, "end": v(-15.37, -108) * mm});
            skLineSegment(sketch, "E88.MirrorCS", {"start": v(15, -120.03) * mm, "end": v(15.02, -108) * mm});
            skCircle(sketch, "E89.MirrorC", {"center": v(0, -120) * mm, "radius": 6 * mm});
            skArc(sketch, "E90.MirrorCS", {"start": v(15, -120.03) * mm, "mid": v(-0.1, -135) * mm, "end": v(-15, -119.83) * mm});
            skLineSegment(sketch, "E91.MirrorCS", {"start": v(-15.37, -108) * mm, "end": v(-33.37, -90) * mm});
            skLineSegment(sketch, "E92.MirrorCS", {"start": v(15.02, -108) * mm, "end": v(33.02, -90) * mm});
            skLineSegment(sketch, "E93.MirrorCS", {"start": v(0, -120) * mm, "end": v(0, -90) * mm, "construction": true});
            skSolve(sketch);
        }
        {
            var Q0;
            Q0=makeQuery(id+"F16.imprint","IMPRINT",FACE,{"disambiguationData":[TD([[makeQuery(id+"F16.imprint","IMPRINT",EDGE,{"derivedFrom":sQuery(id+"F16.wireOp",EDGE,"E80")}),-1.0]])]});
            var Q1;
            Q1=makeQuery(id+"F16.imprint","IMPRINT",FACE,{"disambiguationData":[TD([[makeQuery(id+"F16.imprint","IMPRINT",EDGE,{"derivedFrom":sQuery(id+"F16.wireOp",EDGE,"E87.MirrorCS")}),-1.0]])]});
            var Q2;
            Q2=makeQuery(id+"F16.imprint","IMPRINT",FACE,{"disambiguationData":[TD([[makeQuery(id+"F16.imprint","IMPRINT",EDGE,{"derivedFrom":makeQuery(id+"F1.opExtrude","CAP_EDGE",EDGE,{"disambiguationData":[OSD([sQuery(id+"F0.wireOp",EDGE,"E1.left")])],"isStart":true})}),-1.0]])]});
            var Q3;
            Q3=makeQuery(id+"F2.opExtrude","CAP_FACE",FACE,{"disambiguationData":[OSD([sQuery(id+"F0.wireOp",EDGE,"E12"),sQuery(id+"F0.wireOp",EDGE,"E13"),sQuery(id+"F0.wireOp",EDGE,"E14"),sQuery(id+"F0.wireOp",EDGE,"E15"),sQuery(id+"F0.wireOp",EDGE,"E17.filletArc"),sQuery(id+"F0.wireOp",EDGE,"E18.filletArc"),sQuery(id+"F0.wireOp",EDGE,"E19.filletArc"),sQuery(id+"F0.wireOp",EDGE,"E20.filletArc"),sQuery(id+"F0.wireOp",EDGE,"E25.0"),sQuery(id+"F0.wireOp",EDGE,"E25.1"),sQuery(id+"F0.wireOp",EDGE,"E25.2"),sQuery(id+"F0.wireOp",EDGE,"E25.3"),sQuery(id+"F0.wireOp",EDGE,"E25.4"),sQuery(id+"F0.wireOp",EDGE,"E25.5"),sQuery(id+"F0.wireOp",EDGE,"E25.6"),sQuery(id+"F0.wireOp",EDGE,"E25.7")])],"isStart":false});
            extrude(context, id + "F17", {"entities" : qUnion([Q0, Q1, Q2]), "endBound" : BoundingType.UP_TO_SURFACE, "endBoundEntityFace" : qUnion([Q3]), "depth" : 5 * mm});
        }
    });
